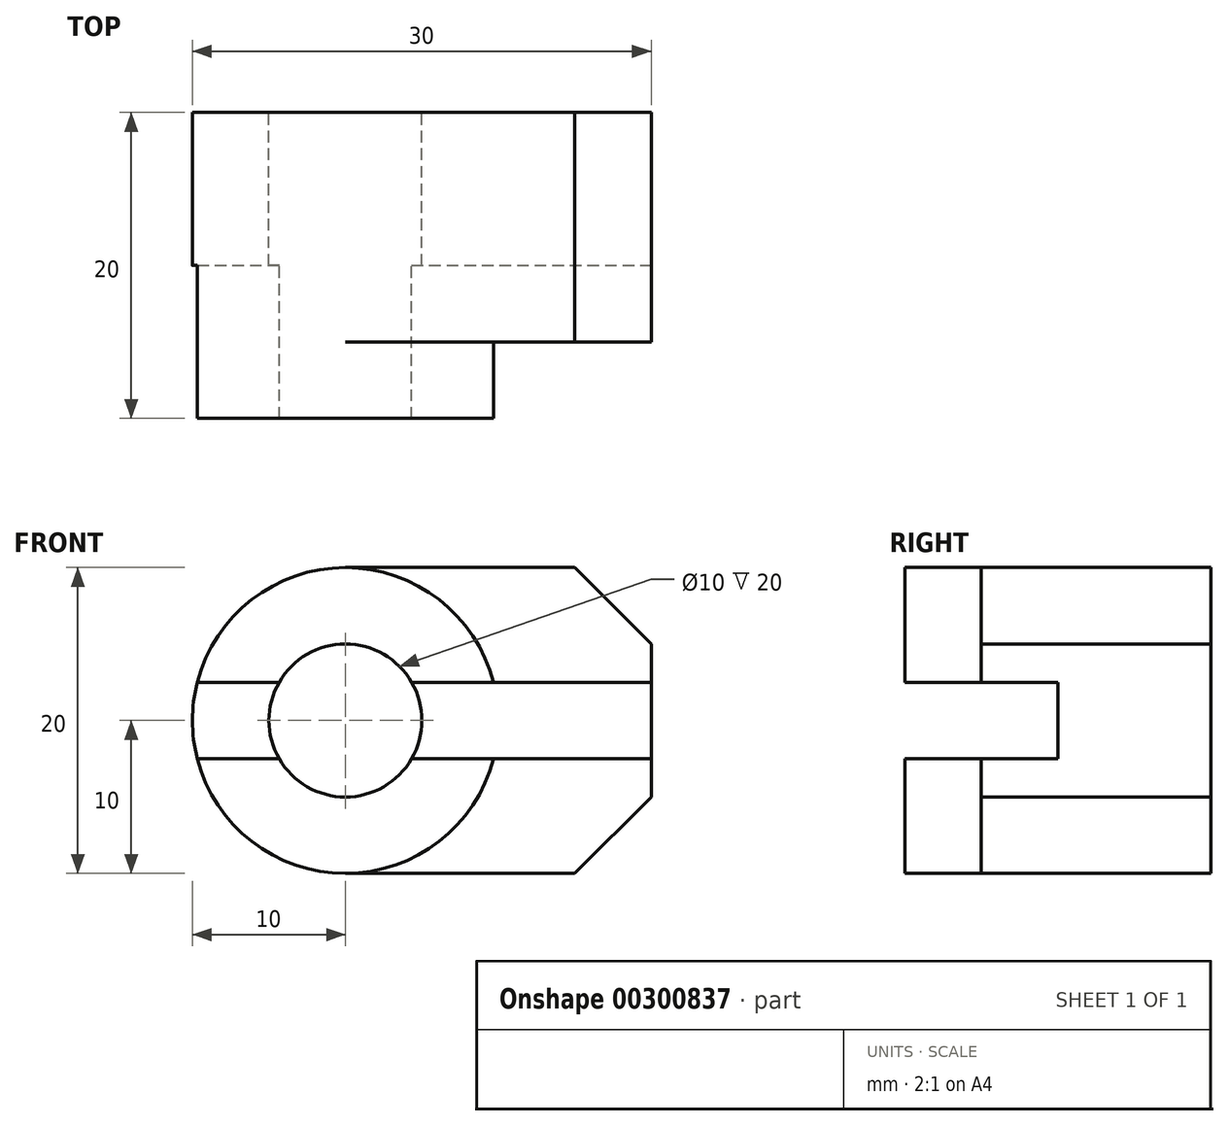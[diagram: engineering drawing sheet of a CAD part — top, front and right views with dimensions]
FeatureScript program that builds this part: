
annotation { "Feature Type Name" : "Feature", "Feature Type Description" : "" }
export const myFeature = defineFeature(function(context is Context, id is Id, definition is map)
    precondition{}
    {
        {
            var Q0;
            Q0=qCreatedBy(makeId("Front.planeOp"),FACE);
            var sketch = newSketch(context, id + "F0", { "sketchPlane" : qUnion([Q0])});
            skCircle(sketch, "E0", {"center": v(0, 0) * mm, "radius": 5 * mm});
            skCircle(sketch, "E1", {"center": v(0, 0) * mm, "radius": 10 * mm});
            skLineSegment(sketch, "E2", {"start": v(0, 10) * mm, "end": v(15, 10) * mm});
            skLineSegment(sketch, "E3", {"start": v(15, 10) * mm, "end": v(20, 5) * mm});
            skLineSegment(sketch, "E4", {"start": v(20, 5) * mm, "end": v(20, -5) * mm});
            skLineSegment(sketch, "E5", {"start": v(20, -5) * mm, "end": v(15, -10) * mm});
            skLineSegment(sketch, "E6", {"start": v(15, -10) * mm, "end": v(0, -10) * mm});
            skSolve(sketch);
        }
        {
            var Q0;
            {var subQ0=sQuery(id+"F0.wireOp",EDGE,"E2");Q0=makeQuery(id+"F0.imprint","IMPRINT",FACE,{"disambiguationData":[TD([[makeQuery(id+"F0.imprint","IMPRINT",EDGE,{"derivedFrom":subQ0}),-1.0]])]});}
            extrude(context, id + "F1", {"entities" : qUnion([Q0]), "oppositeDirection" : true, "depth" : 15 * mm});
        }
        {
            var Q0;
            Q0=makeQuery(id+"F0.imprint","IMPRINT",FACE,{"disambiguationData":[TD([[makeQuery(id+"F0.imprint","IMPRINT",EDGE,{"derivedFrom":sQuery(id+"F0.wireOp",EDGE,"E0")}),-1.0]])]});
            var Q1;
            Q1=makeQuery(id+"F1.opExtrude","CAP_FACE",FACE,{"disambiguationData":[OSD([sQuery(id+"F0.wireOp",EDGE,"E1"),sQuery(id+"F0.wireOp",EDGE,"E2"),sQuery(id+"F0.wireOp",EDGE,"E3"),sQuery(id+"F0.wireOp",EDGE,"E4"),sQuery(id+"F0.wireOp",EDGE,"E5"),sQuery(id+"F0.wireOp",EDGE,"E6")])],"isStart":false});
            extrude(context, id + "F2", {"entities" : qUnion([Q0]), "operationType" : NewBodyOperationType.ADD, "depth" : 5 * mm, "hasSecondDirection" : true, "secondDirectionBound" : SecondDirectionBoundingType.UP_TO_SURFACE, "secondDirectionOppositeDirection" : true, "secondDirectionBoundEntityFace" : qUnion([Q1]), "secondDirectionDepth" : 25 * mm});
        }
        {
            var Q0;
            Q0=makeQuery(id+"F1.opExtrude","SWEPT_FACE",FACE,{"disambiguationData":[OSD([sQuery(id+"F0.wireOp",EDGE,"E4")])]});
            var sketch = newSketch(context, id + "F3", { "sketchPlane" : qUnion([Q0])});
            skPoint(sketch, "E7.firstSnap0", {"position": v(0, 2.5) * mm});
            skLineSegment(sketch, "E7.bottom", {"start": v(-5, 2.5) * mm, "end": v(5, 2.5) * mm});
            skLineSegment(sketch, "E7.top", {"start": v(-5, -2.5) * mm, "end": v(5, -2.5) * mm});
            skLineSegment(sketch, "E7.left", {"start": v(-5, 2.5) * mm, "end": v(-5, -2.5) * mm});
            skLineSegment(sketch, "E7.right", {"start": v(5, 2.5) * mm, "end": v(5, -2.5) * mm});
            skSolve(sketch);
        }
        {
            var Q0;
            Q0 = qSketchRegion(id + "F3", true);
            extrude(context, id + "F4", {"entities" : qUnion([Q0]), "operationType" : NewBodyOperationType.REMOVE, "endBound" : BoundingType.THROUGH_ALL, "oppositeDirection" : true, "depth" : 25 * mm});
        }
    });
